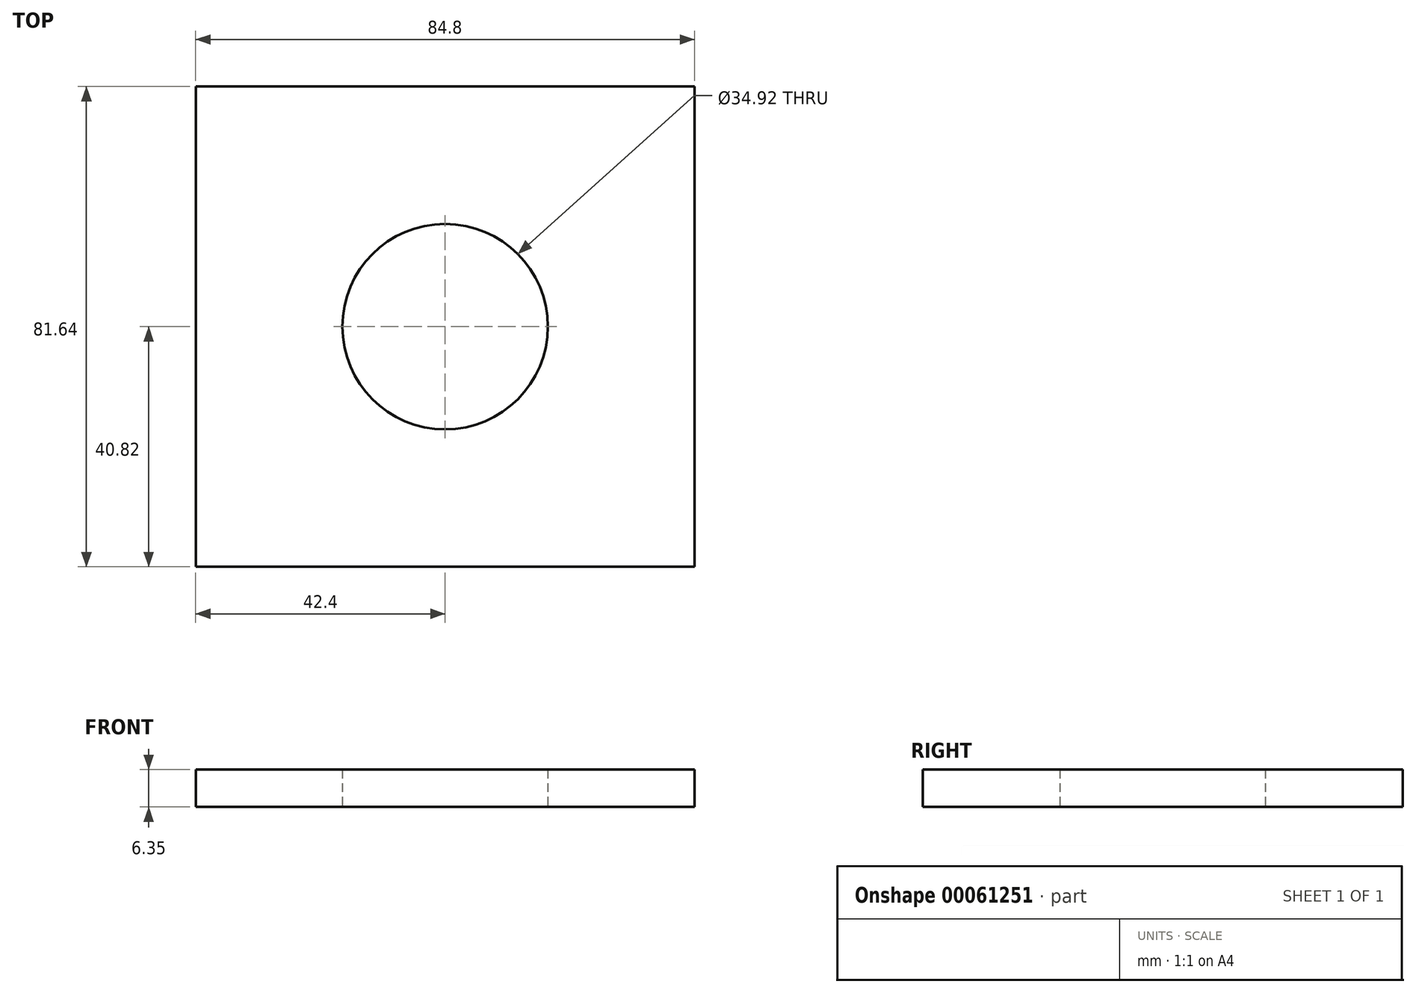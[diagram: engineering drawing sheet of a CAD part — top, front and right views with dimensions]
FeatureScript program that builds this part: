
annotation { "Feature Type Name" : "Feature", "Feature Type Description" : "" }
export const myFeature = defineFeature(function(context is Context, id is Id, definition is map)
    precondition{}
    {
        {
            var Q0;
            Q0=qCreatedBy(makeId("Top.planeOp"),FACE);
            var sketch = newSketch(context, id + "F0", { "sketchPlane" : qUnion([Q0])});
            skCircle(sketch, "E0", {"center": v(0, 0) * mm, "radius": 17.46 * mm});
            skLineSegment(sketch, "E1.rect.bottom", {"start": v(42.4, -40.82) * mm, "end": v(-42.4, -40.82) * mm});
            skLineSegment(sketch, "E1.rect.top", {"start": v(42.4, 40.82) * mm, "end": v(-42.4, 40.82) * mm});
            skLineSegment(sketch, "E1.rect.left", {"start": v(42.4, -40.82) * mm, "end": v(42.4, 40.82) * mm});
            skLineSegment(sketch, "E1.rect.right", {"start": v(-42.4, -40.82) * mm, "end": v(-42.4, 40.82) * mm});
            skSolve(sketch);
        }
        {
            var Q0;
            Q0=makeQuery(id+"F0.imprint","IMPRINT",FACE,{"disambiguationData":[TD([[makeQuery(id+"F0.imprint","IMPRINT",EDGE,{"derivedFrom":sQuery(id+"F0.wireOp",EDGE,"E0")}),-1.0]])]});
            extrude(context, id + "F1", {"entities" : qUnion([Q0]), "depth" : 6.35 * mm});
        }
    });
